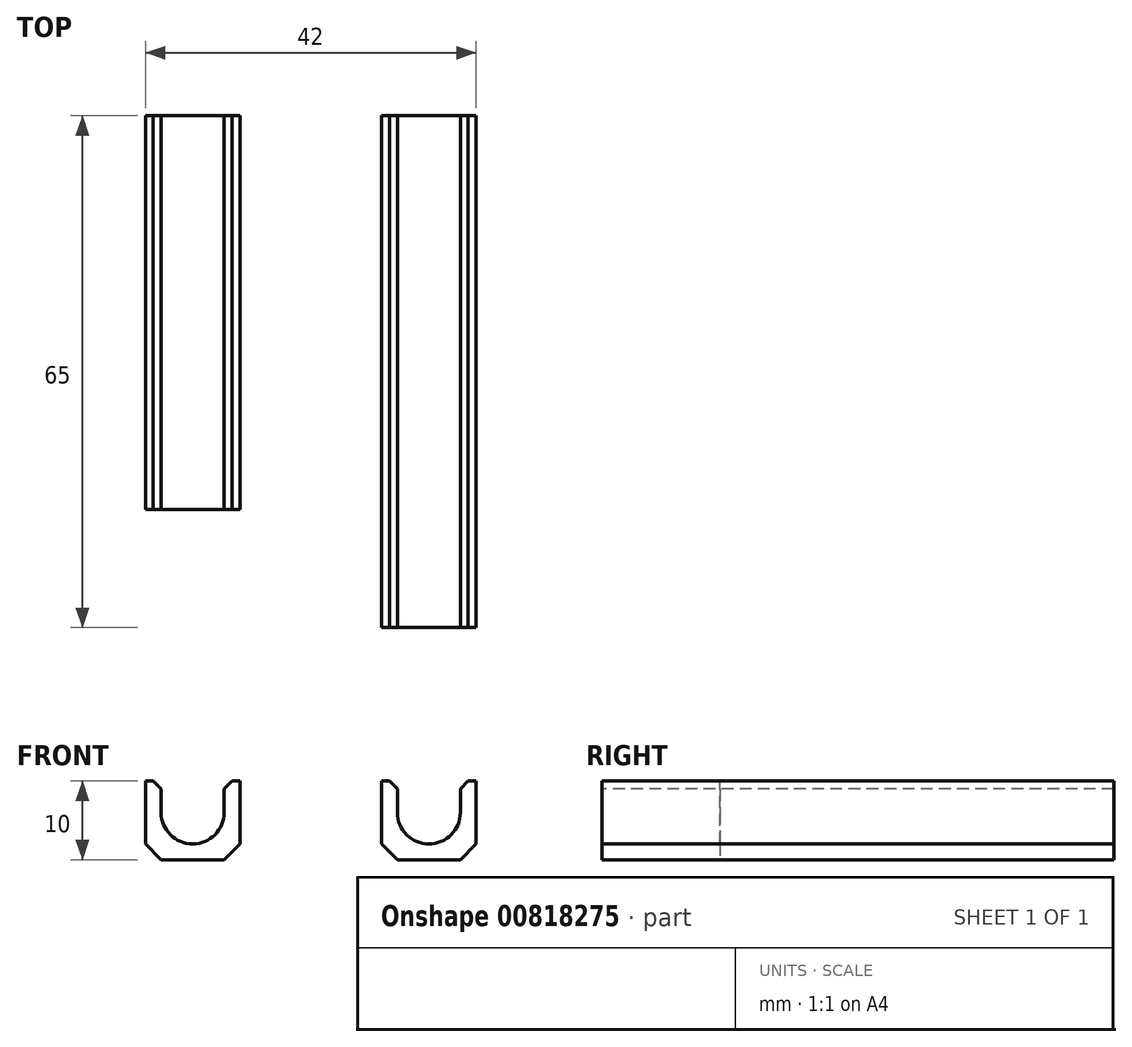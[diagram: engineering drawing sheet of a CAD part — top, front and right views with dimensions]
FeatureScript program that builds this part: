
annotation { "Feature Type Name" : "Feature", "Feature Type Description" : "" }
export const myFeature = defineFeature(function(context is Context, id is Id, definition is map)
    precondition{}
    {
        {
            var Q0;
            Q0=qCreatedBy(makeId("Top.planeOp"),FACE);
            var sketch = newSketch(context, id + "F0", { "sketchPlane" : qUnion([Q0])});
            skLineSegment(sketch, "E0.bottom", {"start": v(0, 0) * mm, "end": v(12, 0) * mm});
            skLineSegment(sketch, "E0.top", {"start": v(0, 6) * mm, "end": v(12, 6) * mm});
            skLineSegment(sketch, "E0.left", {"start": v(0, 0) * mm, "end": v(0, 6) * mm});
            skLineSegment(sketch, "E0.right", {"start": v(12, 0) * mm, "end": v(12, 6) * mm});
            skCircle(sketch, "E1", {"center": v(6, 6) * mm, "radius": 4 * mm});
            skSolve(sketch);
        }
        {
            var Q0;
            Q0=makeQuery(id+"F0.imprint","IMPRINT",FACE,{"disambiguationData":[TD([[makeQuery(id+"F0.imprint","IMPRINT",EDGE,{"derivedFrom":sQuery(id+"F0.wireOp",EDGE,"E0.bottom")}),1.0]])]});
            extrude(context, id + "F1", {"entities" : qUnion([Q0]), "depth" : 50 * mm, "offsetDistance" : 25 * mm});
        }
        {
            var Q0;
            {var subQ0=sQuery(id+"F0.wireOp",EDGE,"E0.top");Q0=makeQuery(id+"F1.opExtrude","SWEPT_FACE",FACE,{"disambiguationData":[OSD([subQ0]),TDD([makeQuery(id+"F0.imprint","IMPRINT",EDGE,{"disambiguationData":[TD([[makeQuery(id+"F0.imprint","INTERSECT",VERTEX,{"derivedFrom":[subQ0,sQuery(id+"F0.wireOp",EDGE,"E0.left")]}),-1.0]])],"derivedFrom":subQ0})])]});}
            var Q1;
            {var subQ0=sQuery(id+"F0.wireOp",EDGE,"E0.top");Q1=makeQuery(id+"F1.opExtrude","SWEPT_FACE",FACE,{"disambiguationData":[OSD([subQ0]),TDD([makeQuery(id+"F0.imprint","IMPRINT",EDGE,{"disambiguationData":[TD([[makeQuery(id+"F0.imprint","INTERSECT",VERTEX,{"derivedFrom":[subQ0,sQuery(id+"F0.wireOp",EDGE,"E0.right")]}),1.0]])],"derivedFrom":subQ0})])]});}
            extrude(context, id + "F2", {"entities" : qUnion([Q0, Q1]), "operationType" : NewBodyOperationType.ADD, "depth" : 4 * mm, "offsetDistance" : 25 * mm});
        }
        {
            var Q0;
            {var subQ0=sQuery(id+"F0.wireOp",EDGE,"E1");var subQ1=sQuery(id+"F0.wireOp",EDGE,"E0.top");Q0=makeQuery(id+"F2.opExtrude","CAP_EDGE",EDGE,{"disambiguationData":[OSD([subQ1,subQ0]),TDD([makeQuery(id+"F1.opExtrude","SWEPT_EDGE",EDGE,{"disambiguationData":[OSD([subQ1,subQ0]),TDD([makeQuery(id+"F0.imprint","INTERSECT",VERTEX,{"disambiguationData":[OD(0.0)],"derivedFrom":[subQ1,subQ0]})])]})])],"isStart":false});}
            var Q1;
            {var subQ0=sQuery(id+"F0.wireOp",EDGE,"E1");var subQ1=sQuery(id+"F0.wireOp",EDGE,"E0.top");Q1=makeQuery(id+"F2.opExtrude","CAP_EDGE",EDGE,{"disambiguationData":[OSD([subQ1,subQ0]),TDD([makeQuery(id+"F1.opExtrude","SWEPT_EDGE",EDGE,{"disambiguationData":[OSD([subQ1,subQ0]),TDD([makeQuery(id+"F0.imprint","INTERSECT",VERTEX,{"disambiguationData":[OD(1.0)],"derivedFrom":[subQ1,subQ0]})])]})])],"isStart":false});}
            chamfer(context, id + "F3", {"entities" : qUnion([Q0, Q1]), "width" : 1 * mm, "tangentPropagation" : true});
        }
        {
            var Q0;
            Q0=makeQuery(id+"F1.opExtrude","SWEPT_EDGE",EDGE,{"disambiguationData":[OSD([sQuery(id+"F0.wireOp",EDGE,"E0.bottom"),sQuery(id+"F0.wireOp",EDGE,"E0.left")])]});
            var Q1;
            Q1=makeQuery(id+"F1.opExtrude","SWEPT_EDGE",EDGE,{"disambiguationData":[OSD([sQuery(id+"F0.wireOp",EDGE,"E0.bottom"),sQuery(id+"F0.wireOp",EDGE,"E0.right")])]});
            chamfer(context, id + "F4", {"entities" : qUnion([Q0, Q1]), "width" : 2 * mm, "tangentPropagation" : true});
        }
        {
            var Q0;
            Q0=makeQuery(id+"F1.opExtrude","SWEPT_BODY",BODY,{"disambiguationData":[OSD([sQuery(id+"F0.wireOp",EDGE,"E0.bottom"),sQuery(id+"F0.wireOp",EDGE,"E0.top"),sQuery(id+"F0.wireOp",EDGE,"E0.left"),sQuery(id+"F0.wireOp",EDGE,"E0.right"),sQuery(id+"F0.wireOp",EDGE,"E1")])]});
            var Q1;
            Q1=makeQuery(id+"F1.opExtrude","CAP_EDGE",EDGE,{"disambiguationData":[OSD([sQuery(id+"F0.wireOp",EDGE,"E0.bottom")])],"isStart":true});
            transform(context, id + "F5", {"entities" : qUnion([Q0]), "transformType" : TransformType.ROTATION, "transformAxis" : qUnion([Q1]), "angle" : 90 * degree, "makeCopy" : false});
        }
        {
            var Q0;
            Q0=makeQuery(id+"F1.opExtrude","SWEPT_BODY",BODY,{"disambiguationData":[OSD([sQuery(id+"F0.wireOp",EDGE,"E0.bottom"),sQuery(id+"F0.wireOp",EDGE,"E0.top"),sQuery(id+"F0.wireOp",EDGE,"E0.left"),sQuery(id+"F0.wireOp",EDGE,"E0.right"),sQuery(id+"F0.wireOp",EDGE,"E1")])]});
            transform(context, id + "F6", {"entities" : qUnion([Q0]), "transformType" : TransformType.TRANSLATION_3D, "dx" : 30 * mm, "dy" : 0 * mm, "dz" : 0 * mm, "makeCopy" : true});
        }
        {
            var Q0;
            {var subQ0=sQuery(id+"F0.wireOp",EDGE,"E0.right");var subQ1=sQuery(id+"F0.wireOp",EDGE,"E0.top");var subQ2=sQuery(id+"F0.wireOp",EDGE,"E1");var subQ3=sQuery(id+"F0.wireOp",EDGE,"E0.left");Q0=makeQuery(id+"F6.opPattern","COPY",FACE,{"derivedFrom":makeQuery(id+"F2.boolean.opBoolean","MERGE",FACE,{"derivedFrom":[makeQuery(id+"F1.opExtrude","CAP_FACE",FACE,{"disambiguationData":[OSD([sQuery(id+"F0.wireOp",EDGE,"E0.bottom"),subQ1,subQ3,subQ0,subQ2])],"isStart":false}),makeQuery(id+"F2.opExtrude","SWEPT_FACE",FACE,{"disambiguationData":[OSD([subQ1]),TDD([makeQuery(id+"F1.opExtrude","CAP_EDGE",EDGE,{"disambiguationData":[OSD([subQ1]),TDD([makeQuery(id+"F0.imprint","IMPRINT",EDGE,{"disambiguationData":[TD([[makeQuery(id+"F0.imprint","INTERSECT",VERTEX,{"derivedFrom":[subQ1,subQ3]}),-1.0]])],"derivedFrom":subQ1})])],"isStart":false})])]}),makeQuery(id+"F2.opExtrude","SWEPT_FACE",FACE,{"disambiguationData":[OSD([subQ1]),TDD([makeQuery(id+"F1.opExtrude","CAP_EDGE",EDGE,{"disambiguationData":[OSD([subQ1]),TDD([makeQuery(id+"F0.imprint","IMPRINT",EDGE,{"disambiguationData":[TD([[makeQuery(id+"F0.imprint","INTERSECT",VERTEX,{"derivedFrom":[subQ1,subQ0]}),1.0]])],"derivedFrom":subQ1})])],"isStart":false})])]})]}),"instanceName":"1"});}
            extrude(context, id + "F7", {"entities" : qUnion([Q0]), "operationType" : NewBodyOperationType.ADD, "depth" : 15 * mm, "offsetDistance" : 25 * mm});
        }
    });
